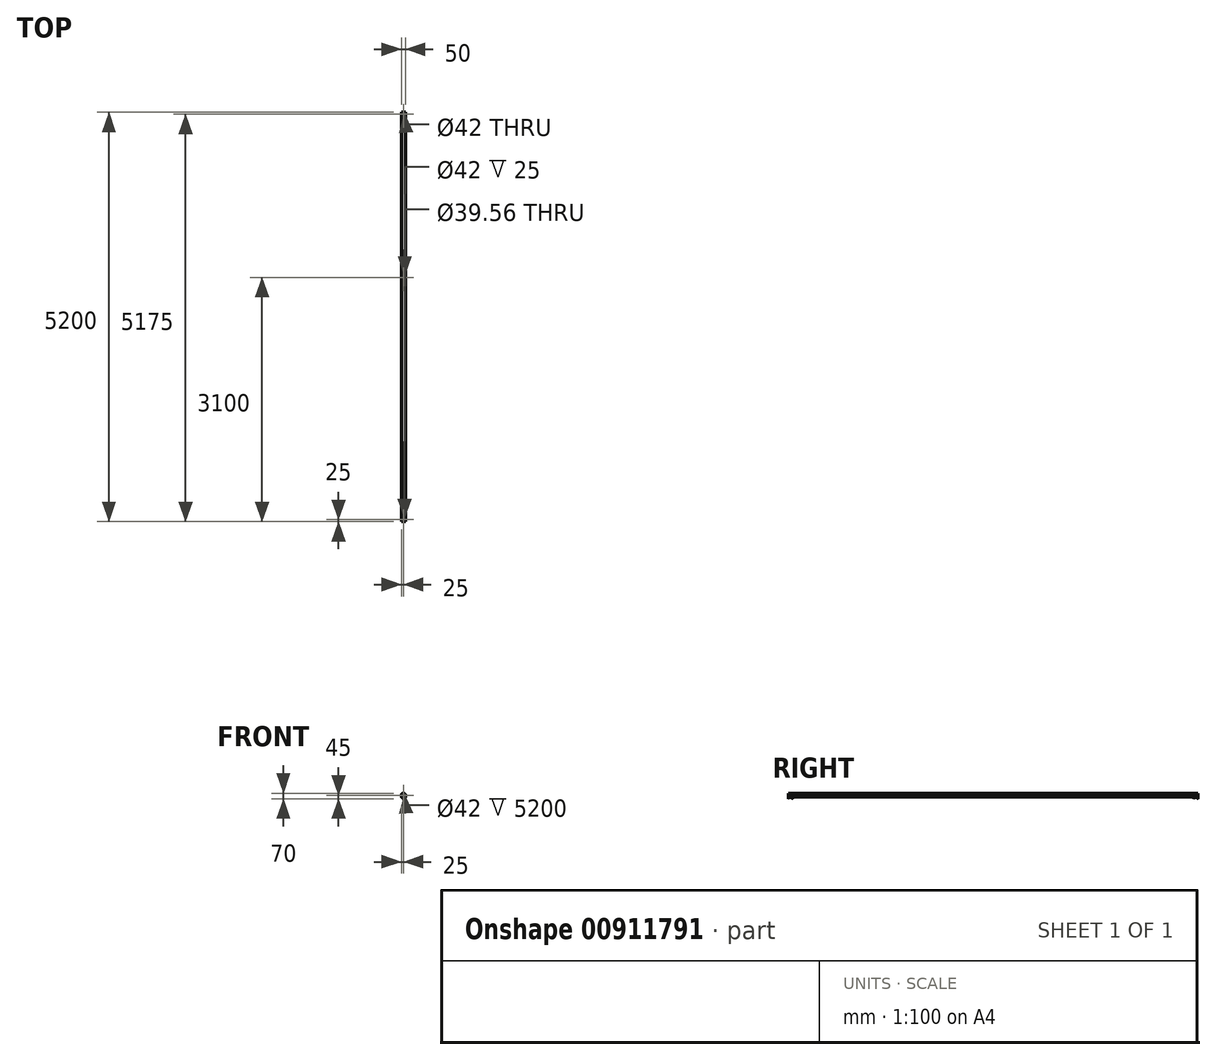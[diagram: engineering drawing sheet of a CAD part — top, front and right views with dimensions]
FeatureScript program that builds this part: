
annotation { "Feature Type Name" : "Feature", "Feature Type Description" : "" }
export const myFeature = defineFeature(function(context is Context, id is Id, definition is map)
    precondition{}
    {
        {
            var Q0;
            Q0=qCreatedBy(makeId("Front.planeOp"),FACE);
            var sketch = newSketch(context, id + "F0", { "sketchPlane" : qUnion([Q0])});
            skCircle(sketch, "E0", {"center": v(0, 0) * mm, "radius": 25 * mm});
            skCircle(sketch, "E1", {"center": v(0, 0) * mm, "radius": 21 * mm});
            skSolve(sketch);
        }
        {
            var Q0;
            Q0=makeQuery(id+"F0.imprint","IMPRINT",FACE,{"disambiguationData":[TD([[makeQuery(id+"F0.imprint","IMPRINT",EDGE,{"derivedFrom":sQuery(id+"F0.wireOp",EDGE,"E0")}),1.0]])]});
            extrude(context, id + "F1", {"entities" : qUnion([Q0]), "depth" : 5200 * mm, "offsetDistance" : 25 * mm});
        }
        {
            var Q0;
            Q0=qCreatedBy(makeId("Top.planeOp"),FACE);
            var sketch = newSketch(context, id + "F2", { "sketchPlane" : qUnion([Q0])});
            skCircle(sketch, "E2", {"center": v(0, -2100) * mm, "radius": 25 * mm});
            skSolve(sketch);
        }
        {
            var Q0;
            Q0=qSketchRegion(id+"F2",true);
            extrude(context, id + "F3", {"entities" : qUnion([Q0]), "operationType" : NewBodyOperationType.ADD, "oppositeDirection" : true, "depth" : 25 * mm, "offsetDistance" : 25 * mm});
        }
        {
            var Q0;
            Q0=qCreatedBy(makeId("Top.planeOp"),FACE);
            var sketch = newSketch(context, id + "F4", { "sketchPlane" : qUnion([Q0])});
            skCircle(sketch, "E3", {"center": v(0, -25) * mm, "radius": 25 * mm});
            skSolve(sketch);
        }
        {
            var Q0;
            Q0=qSketchRegion(id+"F4",true);
            extrude(context, id + "F5", {"entities" : qUnion([Q0]), "operationType" : NewBodyOperationType.ADD, "oppositeDirection" : true, "depth" : 45 * mm, "offsetDistance" : 25 * mm});
        }
        {
            var Q0;
            Q0=qCreatedBy(makeId("Top.planeOp"),FACE);
            var sketch = newSketch(context, id + "F6", { "sketchPlane" : qUnion([Q0])});
            skCircle(sketch, "E4", {"center": v(0, -5175) * mm, "radius": 25 * mm});
            skSolve(sketch);
        }
        {
            var Q0;
            Q0=qSketchRegion(id+"F6",true);
            extrude(context, id + "F7", {"entities" : qUnion([Q0]), "operationType" : NewBodyOperationType.ADD, "oppositeDirection" : true, "depth" : 45 * mm, "offsetDistance" : 25 * mm});
        }
        {
            var Q0;
            Q0=qCreatedBy(makeId("Front.planeOp"),FACE);
            var sketch = newSketch(context, id + "F8", { "sketchPlane" : qUnion([Q0])});
            skCircle(sketch, "E5", {"center": v(0, 0) * mm, "radius": 21 * mm});
            skSolve(sketch);
        }
        {
            var Q0;
            Q0=qSketchRegion(id+"F8",true);
            extrude(context, id + "F9", {"entities" : qUnion([Q0]), "operationType" : NewBodyOperationType.REMOVE, "depth" : 6100 * mm, "offsetDistance" : 25 * mm});
        }
        {
            var Q0;
            Q0=makeQuery(id+"F3.boolean.opBoolean","INTERSECT",EDGE,{"disambiguationData":[OD(3.0)],"derivedFrom":[makeQuery(id+"F1.opExtrude","SWEPT_FACE",FACE,{"disambiguationData":[OSD([sQuery(id+"F0.wireOp",EDGE,"E0")])]}),makeQuery(id+"F3.opExtrude","SWEPT_FACE",FACE,{"disambiguationData":[OSD([sQuery(id+"F2.wireOp",EDGE,"E2")])]})]});
            var Q1;
            Q1=makeQuery(id+"F3.boolean.opBoolean","INTERSECT",EDGE,{"disambiguationData":[OD(2.0)],"derivedFrom":[makeQuery(id+"F1.opExtrude","SWEPT_FACE",FACE,{"disambiguationData":[OSD([sQuery(id+"F0.wireOp",EDGE,"E0")])]}),makeQuery(id+"F3.opExtrude","SWEPT_FACE",FACE,{"disambiguationData":[OSD([sQuery(id+"F2.wireOp",EDGE,"E2")])]})]});
            var Q2;
            Q2=makeQuery(id+"F3.boolean.opBoolean","INTERSECT",EDGE,{"disambiguationData":[OD(0.0)],"derivedFrom":[makeQuery(id+"F1.opExtrude","SWEPT_FACE",FACE,{"disambiguationData":[OSD([sQuery(id+"F0.wireOp",EDGE,"E0")])]}),makeQuery(id+"F3.opExtrude","SWEPT_FACE",FACE,{"disambiguationData":[OSD([sQuery(id+"F2.wireOp",EDGE,"E2")])]})]});
            var Q3;
            Q3=makeQuery(id+"F3.boolean.opBoolean","INTERSECT",EDGE,{"disambiguationData":[OD(1.0)],"derivedFrom":[makeQuery(id+"F1.opExtrude","SWEPT_FACE",FACE,{"disambiguationData":[OSD([sQuery(id+"F0.wireOp",EDGE,"E0")])]}),makeQuery(id+"F3.opExtrude","SWEPT_FACE",FACE,{"disambiguationData":[OSD([sQuery(id+"F2.wireOp",EDGE,"E2")])]})]});
            fillet(context, id + "F10", {"entities" : qUnion([Q0, Q1, Q2, Q3]), "radius" : 5 * mm, "tangentPropagation" : true, "allowEdgeOverflow" : false});
        }
        {
            var Q0;
            Q0=makeQuery(id+"F5.boolean.opBoolean","INTERSECT",EDGE,{"disambiguationData":[OD(0.0)],"derivedFrom":[makeQuery(id+"F1.opExtrude","SWEPT_FACE",FACE,{"disambiguationData":[OSD([sQuery(id+"F0.wireOp",EDGE,"E0")])]}),makeQuery(id+"F5.opExtrude","SWEPT_FACE",FACE,{"disambiguationData":[OSD([sQuery(id+"F4.wireOp",EDGE,"E3")])]})]});
            var Q1;
            Q1=makeQuery(id+"F5.boolean.opBoolean","INTERSECT",EDGE,{"disambiguationData":[OD(2.0)],"derivedFrom":[makeQuery(id+"F1.opExtrude","SWEPT_FACE",FACE,{"disambiguationData":[OSD([sQuery(id+"F0.wireOp",EDGE,"E0")])]}),makeQuery(id+"F5.opExtrude","SWEPT_FACE",FACE,{"disambiguationData":[OSD([sQuery(id+"F4.wireOp",EDGE,"E3")])]})]});
            var Q2;
            Q2=makeQuery(id+"F5.boolean.opBoolean","INTERSECT",EDGE,{"disambiguationData":[OD(1.0)],"derivedFrom":[makeQuery(id+"F1.opExtrude","SWEPT_FACE",FACE,{"disambiguationData":[OSD([sQuery(id+"F0.wireOp",EDGE,"E0")])]}),makeQuery(id+"F5.opExtrude","SWEPT_FACE",FACE,{"disambiguationData":[OSD([sQuery(id+"F4.wireOp",EDGE,"E3")])]})]});
            var Q3;
            Q3=makeQuery(id+"F5.boolean.opBoolean","INTERSECT",EDGE,{"disambiguationData":[OD(3.0)],"derivedFrom":[makeQuery(id+"F1.opExtrude","SWEPT_FACE",FACE,{"disambiguationData":[OSD([sQuery(id+"F0.wireOp",EDGE,"E0")])]}),makeQuery(id+"F5.opExtrude","SWEPT_FACE",FACE,{"disambiguationData":[OSD([sQuery(id+"F4.wireOp",EDGE,"E3")])]})]});
            var Q4;
            Q4=makeQuery(id+"F7.boolean.opBoolean","INTERSECT",EDGE,{"disambiguationData":[OD(1.0)],"derivedFrom":[makeQuery(id+"F1.opExtrude","SWEPT_FACE",FACE,{"disambiguationData":[OSD([sQuery(id+"F0.wireOp",EDGE,"E0")])]}),makeQuery(id+"F7.opExtrude","SWEPT_FACE",FACE,{"disambiguationData":[OSD([sQuery(id+"F6.wireOp",EDGE,"E4")])]})]});
            var Q5;
            Q5=makeQuery(id+"F7.boolean.opBoolean","INTERSECT",EDGE,{"disambiguationData":[OD(3.0)],"derivedFrom":[makeQuery(id+"F1.opExtrude","SWEPT_FACE",FACE,{"disambiguationData":[OSD([sQuery(id+"F0.wireOp",EDGE,"E0")])]}),makeQuery(id+"F7.opExtrude","SWEPT_FACE",FACE,{"disambiguationData":[OSD([sQuery(id+"F6.wireOp",EDGE,"E4")])]})]});
            var Q6;
            Q6=makeQuery(id+"F7.boolean.opBoolean","INTERSECT",EDGE,{"disambiguationData":[OD(2.0)],"derivedFrom":[makeQuery(id+"F1.opExtrude","SWEPT_FACE",FACE,{"disambiguationData":[OSD([sQuery(id+"F0.wireOp",EDGE,"E0")])]}),makeQuery(id+"F7.opExtrude","SWEPT_FACE",FACE,{"disambiguationData":[OSD([sQuery(id+"F6.wireOp",EDGE,"E4")])]})]});
            var Q7;
            Q7=makeQuery(id+"F7.boolean.opBoolean","INTERSECT",EDGE,{"disambiguationData":[OD(0.0)],"derivedFrom":[makeQuery(id+"F1.opExtrude","SWEPT_FACE",FACE,{"disambiguationData":[OSD([sQuery(id+"F0.wireOp",EDGE,"E0")])]}),makeQuery(id+"F7.opExtrude","SWEPT_FACE",FACE,{"disambiguationData":[OSD([sQuery(id+"F6.wireOp",EDGE,"E4")])]})]});
            fillet(context, id + "F11", {"entities" : qUnion([Q0, Q1, Q2, Q3, Q4, Q5, Q6, Q7]), "radius" : 5 * mm, "tangentPropagation" : true, "allowEdgeOverflow" : false});
        }
        {
            var Q0;
            Q0=qCreatedBy(makeId("Right.planeOp"),FACE);
            var sketch = newSketch(context, id + "F12", { "sketchPlane" : qUnion([Q0])});
            skLineSegment(sketch, "E6", {"start": v(0, -45.47) * mm, "end": v(-50, -45.47) * mm});
            skArc(sketch, "E7", {"start": v(0, -45.47) * mm, "mid": v(-25, -26.47) * mm, "end": v(-50, -45.47) * mm});
            skSolve(sketch);
        }
        {
            var Q0;
            Q0=qSketchRegion(id+"F12",true);
            extrude(context, id + "F13", {"entities" : qUnion([Q0]), "operationType" : NewBodyOperationType.REMOVE, "depth" : 25 * mm, "offsetDistance" : 25 * mm, "hasSecondDirection" : true, "secondDirectionOppositeDirection" : true, "secondDirectionDepth" : 25 * mm});
        }
        {
            var Q0;
            Q0=qCreatedBy(makeId("Right.planeOp"),FACE);
            var sketch = newSketch(context, id + "F14", { "sketchPlane" : qUnion([Q0])});
            skLineSegment(sketch, "E8", {"start": v(-5200, -45) * mm, "end": v(-5150, -45) * mm});
            skArc(sketch, "E9", {"start": v(-5150, -45) * mm, "mid": v(-5175, -26) * mm, "end": v(-5200, -45) * mm});
            skPoint(sketch, "E10", {"position": v(-5175, -45) * mm});
            skSolve(sketch);
        }
        {
            var Q0;
            Q0=qSketchRegion(id+"F14",true);
            extrude(context, id + "F15", {"entities" : qUnion([Q0]), "operationType" : NewBodyOperationType.REMOVE, "depth" : 25 * mm, "offsetDistance" : 25 * mm, "hasSecondDirection" : true, "secondDirectionOppositeDirection" : true, "secondDirectionDepth" : 25 * mm});
        }
        {
            var Q0;
            Q0=qCreatedBy(makeId("Top.planeOp"),FACE);
            var sketch = newSketch(context, id + "F16", { "sketchPlane" : qUnion([Q0])});
            skCircle(sketch, "E11", {"center": v(0, -25) * mm, "radius": 21 * mm});
            skSolve(sketch);
        }
        {
            var Q0;
            Q0=qSketchRegion(id+"F16",true);
            extrude(context, id + "F17", {"entities" : qUnion([Q0]), "operationType" : NewBodyOperationType.REMOVE, "oppositeDirection" : true, "depth" : 50 * mm, "offsetDistance" : 25 * mm});
        }
        {
            var Q0;
            Q0=makeQuery(id+"F3.opExtrude","CAP_FACE",FACE,{"disambiguationData":[OSD([sQuery(id+"F2.wireOp",EDGE,"E2")])],"isStart":false});
            var sketch = newSketch(context, id + "F18", { "sketchPlane" : qUnion([Q0])});
            skCircle(sketch, "E12", {"center": v(0, 2100) * mm, "radius": 21 * mm});
            skSolve(sketch);
        }
        {
            var Q0;
            Q0=qSketchRegion(id+"F18",true);
            extrude(context, id + "F19", {"entities" : qUnion([Q0]), "operationType" : NewBodyOperationType.REMOVE, "oppositeDirection" : true, "depth" : 25 * mm, "offsetDistance" : 25 * mm});
        }
        {
            var Q0;
            Q0=qCreatedBy(makeId("Top.planeOp"),FACE);
            var sketch = newSketch(context, id + "F20", { "sketchPlane" : qUnion([Q0])});
            skCircle(sketch, "E13", {"center": v(0, -5175) * mm, "radius": 19.78 * mm});
            skSolve(sketch);
        }
        {
            var Q0;
            Q0=qSketchRegion(id+"F20",true);
            extrude(context, id + "F21", {"entities" : qUnion([Q0]), "operationType" : NewBodyOperationType.REMOVE, "oppositeDirection" : true, "depth" : 60 * mm, "offsetDistance" : 25 * mm});
        }
    });
